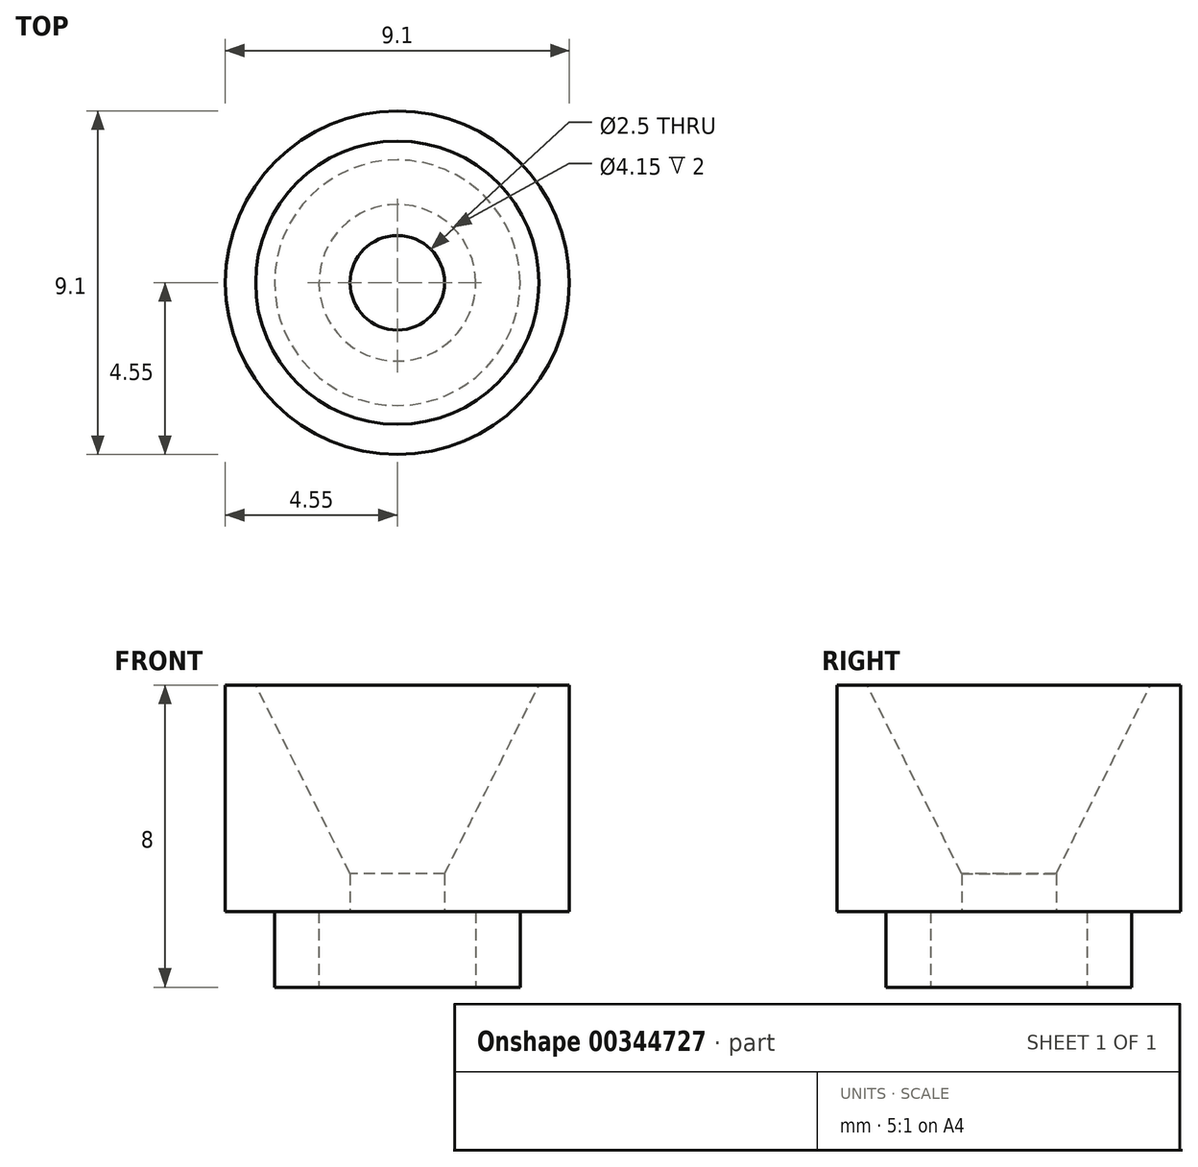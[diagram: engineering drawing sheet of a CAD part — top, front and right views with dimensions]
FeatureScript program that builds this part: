
annotation { "Feature Type Name" : "Feature", "Feature Type Description" : "" }
export const myFeature = defineFeature(function(context is Context, id is Id, definition is map)
    precondition{}
    {
        {
            var Q0;
            Q0=qCreatedBy(makeId("Top.planeOp"),FACE);
            var sketch = newSketch(context, id + "F0", { "sketchPlane" : qUnion([Q0])});
            skCircle(sketch, "E0", {"center": v(0, 0) * mm, "radius": 4.55 * mm});
            skCircle(sketch, "E1", {"center": v(0, 0) * mm, "radius": 1.25 * mm});
            skSolve(sketch);
        }
        {
            var Q0;
            Q0=makeQuery(id+"F0.imprint","IMPRINT",FACE,{"disambiguationData":[TD([[makeQuery(id+"F0.imprint","IMPRINT",EDGE,{"derivedFrom":sQuery(id+"F0.wireOp",EDGE,"E0")}),1.0]])]});
            extrude(context, id + "F1", {"entities" : qUnion([Q0]), "depth" : 8 * mm});
        }
        {
            var Q0;
            Q0=makeQuery(id+"F1.opExtrude","CAP_EDGE",EDGE,{"disambiguationData":[OSD([sQuery(id+"F0.wireOp",EDGE,"E1")])],"isStart":false});
            chamfer(context, id + "F2", {"entities" : qUnion([Q0]), "chamferType" : ChamferType.TWO_OFFSETS, "width1" : 5 * mm, "oppositeDirection" : false, "width2" : 2.5 * mm, "tangentPropagation" : true});
        }
        {
            var Q0;
            Q0=makeQuery(id+"F1.opExtrude","CAP_FACE",FACE,{"disambiguationData":[OSD([sQuery(id+"F0.wireOp",EDGE,"E0"),sQuery(id+"F0.wireOp",EDGE,"E1")])],"isStart":true});
            var sketch = newSketch(context, id + "F3", { "sketchPlane" : qUnion([Q0])});
            skCircle(sketch, "E2", {"center": v(0, 0) * mm, "radius": 2.08 * mm});
            skCircle(sketch, "E3", {"center": v(0, 0) * mm, "radius": 3.25 * mm});
            skSolve(sketch);
        }
        {
            var Q0;
            Q0=makeQuery(id+"F3.imprint","IMPRINT",FACE,{"disambiguationData":[TD([[makeQuery(id+"F3.imprint","IMPRINT",EDGE,{"derivedFrom":sQuery(id+"F3.wireOp",EDGE,"E2")}),1.0]])]});
            var Q1;
            Q1=makeQuery(id+"F3.imprint","IMPRINT",FACE,{"disambiguationData":[TD([[makeQuery(id+"F3.imprint","IMPRINT",EDGE,{"derivedFrom":sQuery(id+"F3.wireOp",EDGE,"E3")}),-1.0]])]});
            extrude(context, id + "F4", {"entities" : qUnion([Q0, Q1]), "operationType" : NewBodyOperationType.REMOVE, "oppositeDirection" : true, "depth" : 2 * mm});
        }
    });
